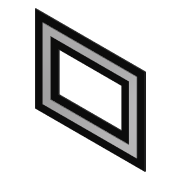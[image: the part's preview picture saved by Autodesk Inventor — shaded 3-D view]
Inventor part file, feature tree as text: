
AUTODESK INVENTOR PART (.ipt)
format: ipt  version: 2012 (Build 160160000, 160)  size: 88,064 bytes
history: native  units: in
note: dims shown in document units (in); Inventor stores cm internally (conversion verified against a paired STEP export)
features: extrude x2, sketch x1
ambient origin geometry x8: Origin, YZ Plane, XZ Plane, XY Plane, X Axis, Y Axis, Z Axis, Center Point
bodies: Solid1 (feature_tree)
feature tree (3):
  sketch  "Sketch1"  dims[d2=2.0in d3=2.0in d4=2.0in d5=0.188in d6=0.0in d7=0.3125in d8=0.0in d9=18.0in d10=24.0in]
  extrude  "Extrusion1"  Depth=2.0in
  extrude  "Extrusion2"  Depth=2.0in
